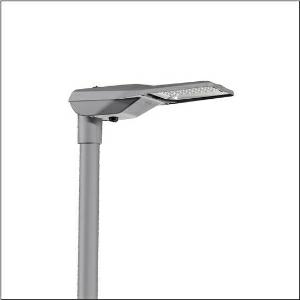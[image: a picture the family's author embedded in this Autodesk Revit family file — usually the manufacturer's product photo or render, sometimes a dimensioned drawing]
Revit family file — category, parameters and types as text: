
# Revit family: streetlight_sl_21_iq_mini___st1_0a_5xe2d51y08gb_2a2c
name_source: partatom
category: Lighting Fixtures
units: mm (PartAtom-declared; Revit-internal decimal feet)

## family parameters
Cut with Voids When Loaded = No
Host = Face
Light Source = No
Part Type = Normal
Room Calculation Point = No
Round Connector Dimension = Use Diameter
Shared = No

## types (1)
- --- (1 x LED, 5260 lm, 39.8 W, 3000K)
    Apparent Load = 40 VA
    CIE Flux Codes = 37 72 97 100 100
    Color Rendering = 80
    Color Temperature = 3000K
    Default Elevation = 1800 mm
    Description = Streetlight SL 21 iQ mini, mast luminaire, primary light control with lens, of PMMA, primary optical cover: cover, of toughened safety glass, transparent, light distribution: ST1.0a, light emission: direct distribution, primary light characteristic: asymmetric, installation type: post-top, side-entry, LED, High Power LED, rated luminous flux: 5.260lm, luminous efficacy: 132lm/W, light colour: 830, colour temperature: 3000K, control gear: iQ-Street Remote, D4i with power reduction, control: pre-setting: logarithmic dimming characteristic, Street-Remote, Auto-Match, Temp-Guard, Lumen-Switch, Night-Set, Smart-Wire, Light-Fading, Desk-Remote (wireless, voltage-free reading and setting of iQ features in the workshop via application-optimized NFC function/RFID function), optimised constant luminous flux control (CLO 2.0), mains connection: 220..240V, AC, 50/60Hz, start of lifetime: 40W, end of service life: 41W, reduction: 18W, luminaire housing, of diecast aluminium, powder-coated, SITECO metallic grey (DB 702S), corrosivity category C5 high according to DIN EN ISO 12944, please order mast flange separately, inclination adjustable: 0°, 5°, 10°, 15°, sealing non-destructively replaceable, multi-level sealing system, length: 628mm, width: 235mm, height: 110mm, mast flange for spigot size: 42mm (side-entry): 5XC10008XM4, 60/48mm (side-entry/post-top): 5XC10108XM2, 76/60mm (side-entry/post-top): 5XC10108XM1, mounting height: 4..8m, Smart Interface below and above, protection rating (complete): IP66, insulation class (complete): insulation class II (safety insulation), certification: CE, ENEC, ENEC+, VDE, impact resistance: IK10, permissible operating ambient temperature for outdoor applications: -40..+50°C, standard-compliant lighting for roads and squares, packaging unit: 1 piece

Light Distribution: ST1.0a
    Height = 110 mm
    Lamp = 1 x LED
    Lamp Light Flux = 5260 lm
    Lamp Power = 39.8 W
    Lamp count = 1
    Length = 625 mm
    Luminous efficacy = 132 lm/W
    Manufacturer = Siteco
    ModVariant = No
    Model = 5XE2D51Y08GB
    Number of Poles = 1
    OnlyDefault = Yes
    Power Factor = 1
    Product Name = Streetlight SL 21 iQ mini | ST1.0a
    Product group = mast luminaire | pylon top
    ProductGroupID = 6100
    Protection Class = Protection class II
    Protection Degree = IP 66
    RLX_Detail_Level = 1
    RLX_Emergency_Light_Flux = 0 lm
    RLX_Emergency_Type = 0
    RLX_Emergency_Type_DB = No
    RlxData = <blob elided: 92581 chars, md5=2e678a69>
    Socket = socket
    Standby Power = 0 W
    System Light Flux = 5260 lm
    System Power = 40 W
    Type Comments = factory setting: luminous flux: 100 % | dim-lin: 254 | 800 mA
    Type Image = l_1003514.jpg
    URL = http://relux.com
    VarID = @adj_114959
    Voltage = 0 V
    Weight = 0.00 kg
    Width = 234 mm

## geometry (parser evidence)
native form markers: Blend x4, Sweep x9
no freeform markers — native parametric forms only
